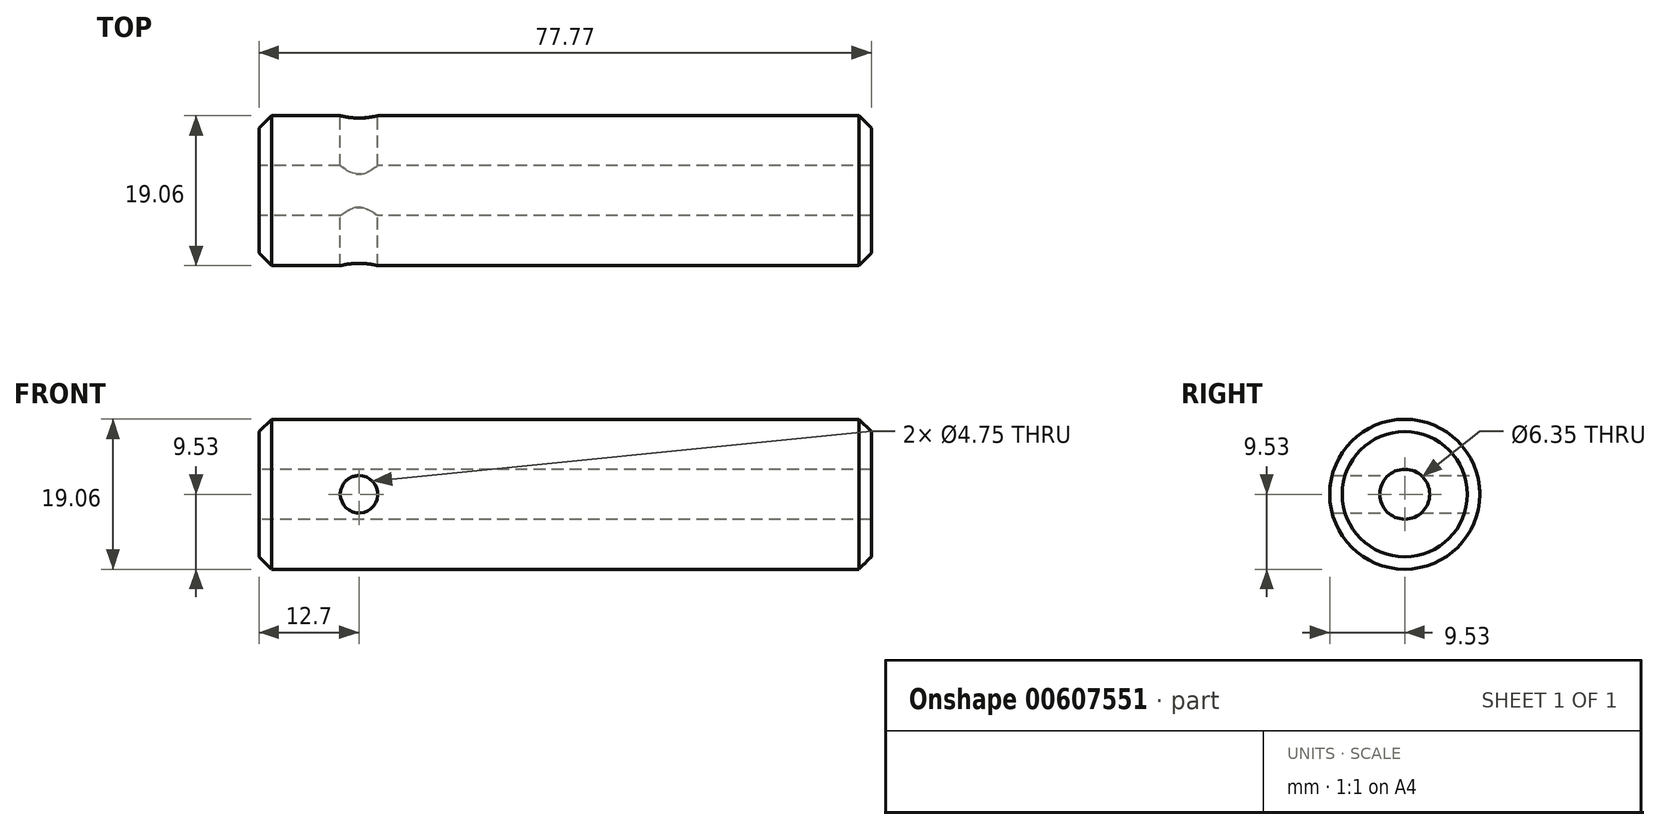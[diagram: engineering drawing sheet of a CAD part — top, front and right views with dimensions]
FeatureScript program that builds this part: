
annotation { "Feature Type Name" : "Feature", "Feature Type Description" : "" }
export const myFeature = defineFeature(function(context is Context, id is Id, definition is map)
    precondition{}
    {
        {
            var Q0;
            Q0=qCreatedBy(makeId("Right.planeOp"),FACE);
            var sketch = newSketch(context, id + "F0", { "sketchPlane" : qUnion([Q0])});
            skCircle(sketch, "E0", {"center": v(0, 0) * mm, "radius": 9.53 * mm});
            skCircle(sketch, "E1", {"center": v(0, 0) * mm, "radius": 3.18 * mm});
            skSolve(sketch);
        }
        {
            var Q0;
            Q0=makeQuery(id+"F0.imprint","IMPRINT",FACE,{"disambiguationData":[TD([[makeQuery(id+"F0.imprint","IMPRINT",EDGE,{"derivedFrom":sQuery(id+"F0.wireOp",EDGE,"E0")}),1.0]])]});
            extrude(context, id + "F1", {"entities" : qUnion([Q0]), "depth" : 77.77 * mm, "offsetDistance" : 25.4 * mm});
        }
        {
            var Q0;
            Q0=qCreatedBy(makeId("Front.planeOp"),FACE);
            var sketch = newSketch(context, id + "F2", { "sketchPlane" : qUnion([Q0])});
            skLineSegment(sketch, "E2", {"start": v(0, 0) * mm, "end": v(12.7, 0) * mm});
            skCircle(sketch, "E3", {"center": v(12.7, 0) * mm, "radius": 2.37 * mm});
            skSolve(sketch);
        }
        {
            var Q0;
            Q0=makeQuery(id+"F2.imprint","IMPRINT",FACE,{"disambiguationData":[TD([[makeQuery(id+"F2.imprint","IMPRINT",EDGE,{"derivedFrom":sQuery(id+"F2.wireOp",EDGE,"E3")}),1.0]])]});
            extrude(context, id + "F3", {"entities" : qUnion([Q0]), "operationType" : NewBodyOperationType.REMOVE, "depth" : 9.52 * mm, "offsetDistance" : 25.4 * mm, "hasSecondDirection" : true, "secondDirectionOppositeDirection" : true, "secondDirectionDepth" : 9.52 * mm});
        }
        {
            var Q0;
            Q0=makeQuery(id+"F1.opExtrude","CAP_EDGE",EDGE,{"disambiguationData":[OSD([sQuery(id+"F0.wireOp",EDGE,"E0")])],"isStart":true});
            var Q1;
            Q1=makeQuery(id+"F1.opExtrude","CAP_EDGE",EDGE,{"disambiguationData":[OSD([sQuery(id+"F0.wireOp",EDGE,"E0")])],"isStart":false});
            chamfer(context, id + "F4", {"entities" : qUnion([Q0, Q1]), "chamferType" : ChamferType.OFFSET_ANGLE, "width" : 1.57 * mm, "oppositeDirection" : false, "angle" : 45 * degree});
        }
    });
